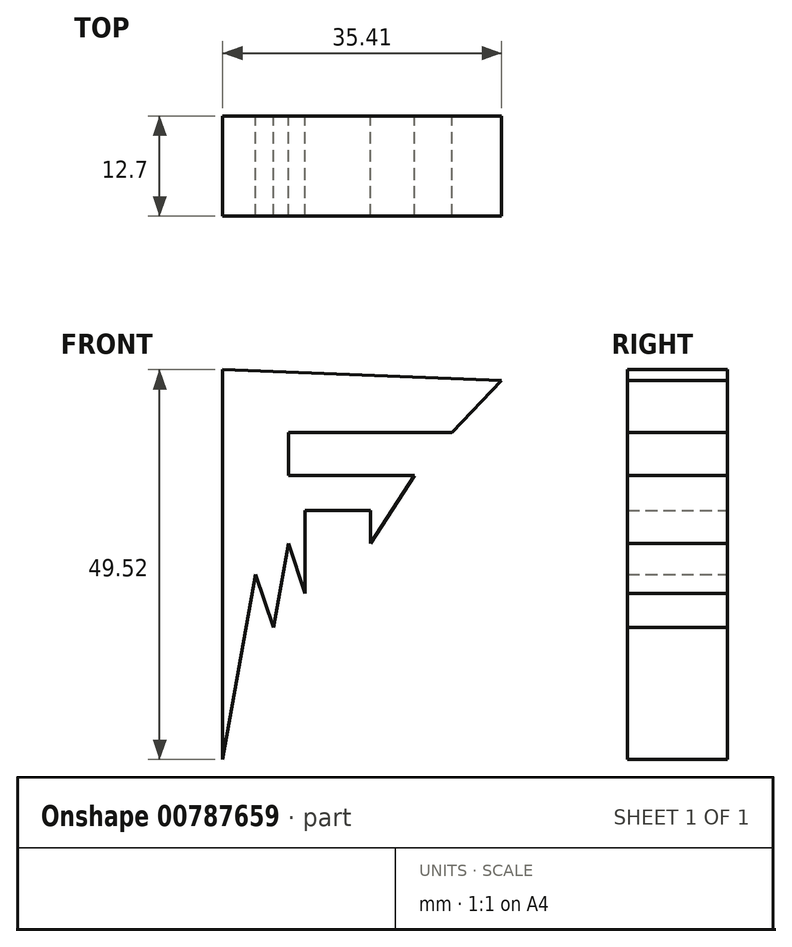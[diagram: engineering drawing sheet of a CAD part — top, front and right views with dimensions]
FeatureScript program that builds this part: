
annotation { "Feature Type Name" : "Feature", "Feature Type Description" : "" }
export const myFeature = defineFeature(function(context is Context, id is Id, definition is map)
    precondition{}
    {
        {
            var Q0;
            Q0=qCreatedBy(makeId("Front.planeOp"),FACE);
            var sketch = newSketch(context, id + "F0", { "sketchPlane" : qUnion([Q0])});
            skLineSegment(sketch, "E0", {"start": v(-42.1, 11.33) * mm, "end": v(-42.1, -38.19) * mm});
            skLineSegment(sketch, "E1", {"start": v(-42.1, -38.19) * mm, "end": v(-37.9, -14.69) * mm});
            skLineSegment(sketch, "E2", {"start": v(-37.9, -14.69) * mm, "end": v(-35.67, -21.4) * mm});
            skLineSegment(sketch, "E3", {"start": v(-35.67, -21.4) * mm, "end": v(-33.77, -10.76) * mm});
            skLineSegment(sketch, "E4", {"start": v(-33.77, -10.76) * mm, "end": v(-31.66, -17.08) * mm});
            skLineSegment(sketch, "E5", {"start": v(-31.66, -17.08) * mm, "end": v(-31.66, -6.57) * mm});
            skLineSegment(sketch, "E6", {"start": v(-31.66, -6.57) * mm, "end": v(-23.36, -6.57) * mm});
            skLineSegment(sketch, "E7", {"start": v(-23.36, -6.57) * mm, "end": v(-23.36, -10.76) * mm});
            skLineSegment(sketch, "E8", {"start": v(-23.36, -10.76) * mm, "end": v(-17.76, -2.1) * mm});
            skLineSegment(sketch, "E9", {"start": v(-17.76, -2.1) * mm, "end": v(-33.77, -2.1) * mm});
            skLineSegment(sketch, "E10", {"start": v(-33.77, -2.1) * mm, "end": v(-33.77, 3.36) * mm});
            skLineSegment(sketch, "E11", {"start": v(-33.77, 3.36) * mm, "end": v(-13.01, 3.36) * mm});
            skLineSegment(sketch, "E12", {"start": v(-13.01, 3.36) * mm, "end": v(-6.7, 9.97) * mm});
            skLineSegment(sketch, "E13", {"start": v(-6.7, 9.97) * mm, "end": v(-42.1, 11.33) * mm});
            skSolve(sketch);
        }
        {
            var Q0;
            Q0=makeQuery(id+"F0.imprint","IMPRINT",FACE,{"disambiguationData":[TD([[makeQuery(id+"F0.imprint","IMPRINT",EDGE,{"derivedFrom":sQuery(id+"F0.wireOp",EDGE,"E0")}),1.0]])]});
            extrude(context, id + "F1", {"entities" : qUnion([Q0]), "depth" : 12.7 * mm, "offsetDistance" : 25.4 * mm});
        }
    });
